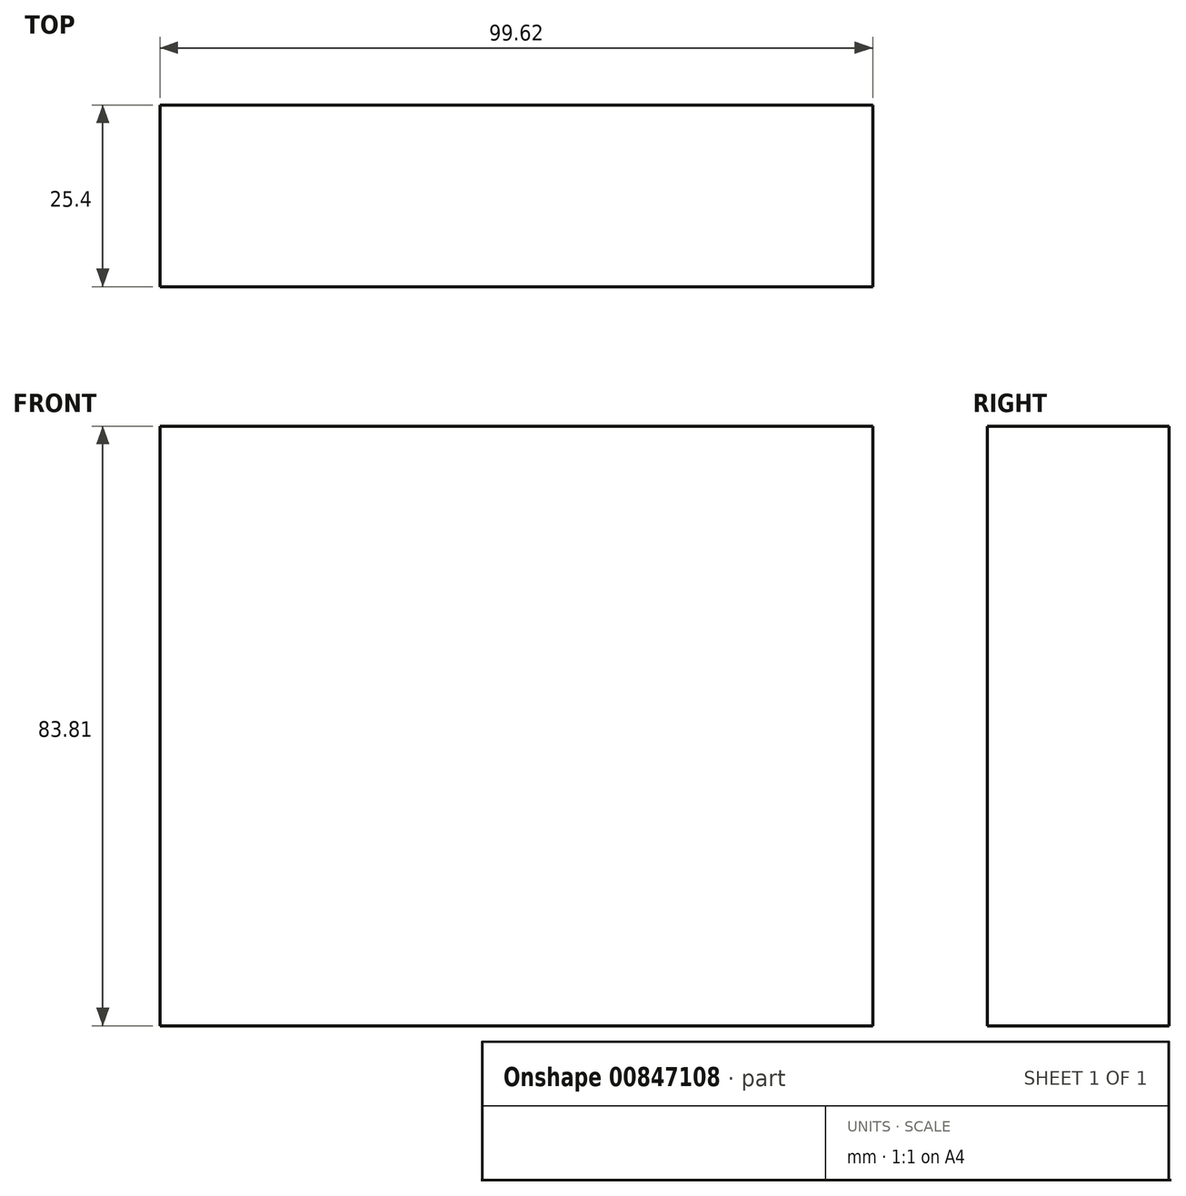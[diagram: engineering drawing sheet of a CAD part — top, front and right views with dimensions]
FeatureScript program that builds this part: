
annotation { "Feature Type Name" : "Feature", "Feature Type Description" : "" }
export const myFeature = defineFeature(function(context is Context, id is Id, definition is map)
    precondition{}
    {
        {
            var Q0;
            Q0=qCreatedBy(makeId("Front.planeOp"),FACE);
            var sketch = newSketch(context, id + "F0", { "sketchPlane" : qUnion([Q0])});
            skLineSegment(sketch, "E0.bottom", {"start": v(-49.26, 44.99) * mm, "end": v(50.36, 44.99) * mm});
            skLineSegment(sketch, "E0.top", {"start": v(-49.26, -38.82) * mm, "end": v(50.36, -38.82) * mm});
            skLineSegment(sketch, "E0.left", {"start": v(-49.26, 44.99) * mm, "end": v(-49.26, -38.82) * mm});
            skLineSegment(sketch, "E0.right", {"start": v(50.36, 44.99) * mm, "end": v(50.36, -38.82) * mm});
            skSolve(sketch);
        }
        {
            var Q0;
            Q0=makeQuery(id+"F0.imprint","IMPRINT",FACE,{"disambiguationData":[TD([[makeQuery(id+"F0.imprint","IMPRINT",EDGE,{"derivedFrom":sQuery(id+"F0.wireOp",EDGE,"E0.bottom")}),-1.0]])]});
            extrude(context, id + "F1", {"entities" : qUnion([Q0]), "depth" : 25.4 * mm, "offsetDistance" : 25.4 * mm});
        }
    });
